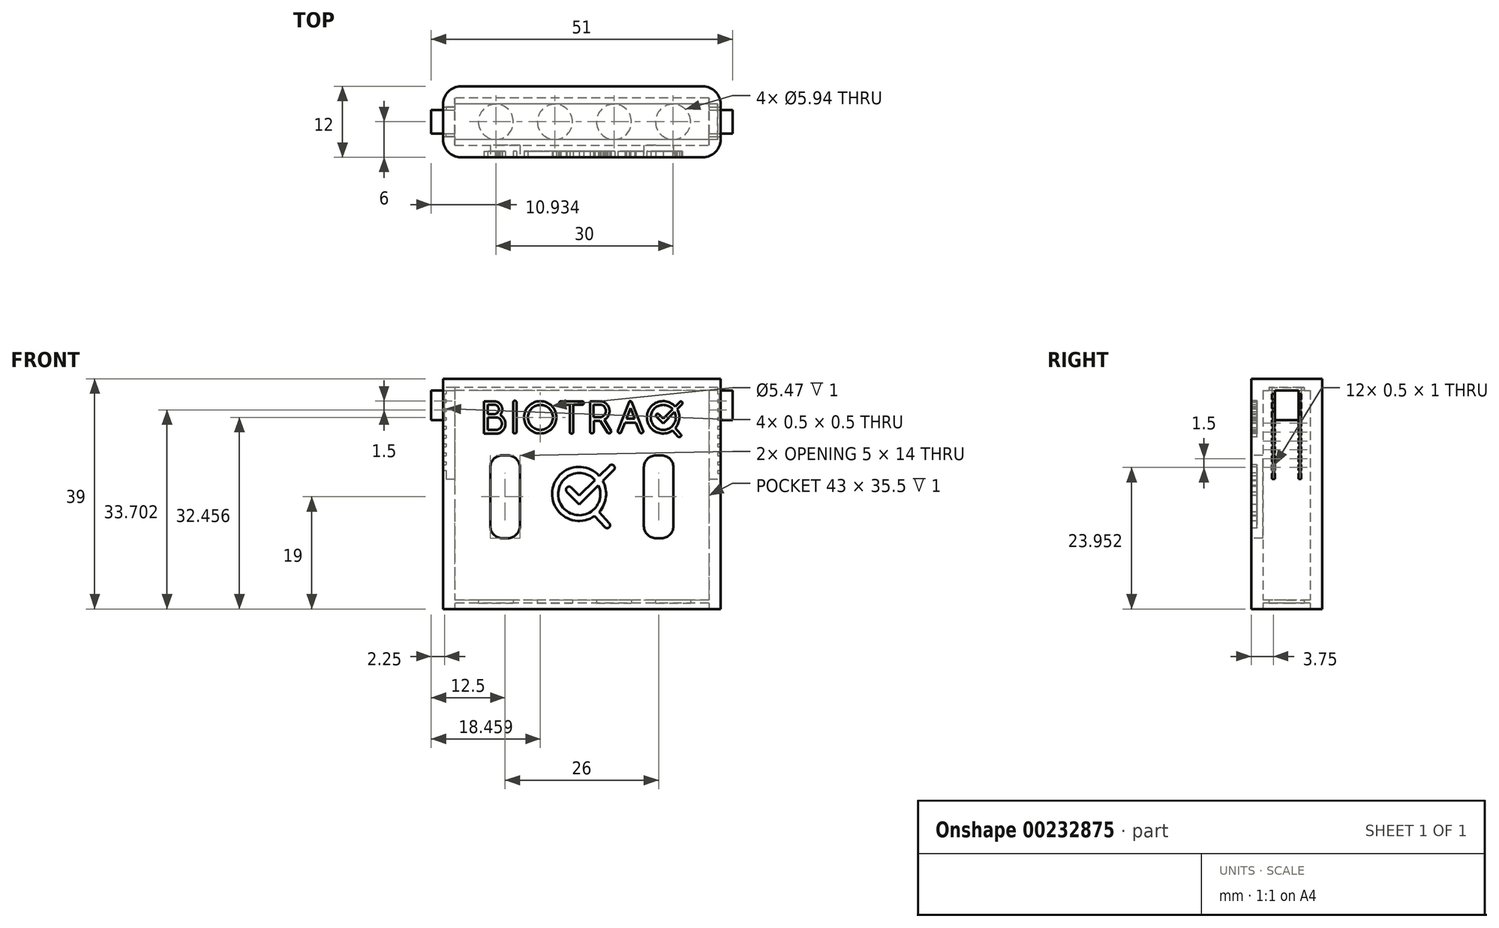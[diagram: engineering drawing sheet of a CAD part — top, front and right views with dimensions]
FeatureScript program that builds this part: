
annotation { "Feature Type Name" : "Feature", "Feature Type Description" : "" }
export const myFeature = defineFeature(function(context is Context, id is Id, definition is map)
    precondition{}
    {
        {
            var Q0;
            Q0=qCreatedBy(makeId("Front.planeOp"),FACE);
            var sketch = newSketch(context, id + "F0", { "sketchPlane" : qUnion([Q0])});
            skLineSegment(sketch, "E0.bottom", {"start": v(-47, 0) * mm, "end": v(0, 0) * mm});
            skLineSegment(sketch, "E0.top", {"start": v(-47, -37) * mm, "end": v(0, -37) * mm});
            skLineSegment(sketch, "E0.left", {"start": v(-47, 0) * mm, "end": v(-47, -37) * mm});
            skLineSegment(sketch, "E0.right", {"start": v(0, 0) * mm, "end": v(0, -37) * mm});
            skSolve(sketch);
        }
        {
            var Q0;
            Q0 = qSketchRegion(id + "F0", true);
            extrude(context, id + "F1", {"entities" : qUnion([Q0]), "depth" : 12 * mm});
        }
        {
            var Q0;
            Q0=makeQuery(id+"F1.opExtrude","SWEPT_FACE",FACE,{"disambiguationData":[OSD([sQuery(id+"F0.wireOp",EDGE,"E0.bottom")])]});
            shell(context, id + "F2", {"entities" : qUnion([Q0]), "thickness" : 2 * mm});
        }
        {
            var Q0;
            Q0=makeQuery(id+"F1.opExtrude","CAP_FACE",FACE,{"disambiguationData":[OSD([sQuery(id+"F0.wireOp",EDGE,"E0.bottom"),sQuery(id+"F0.wireOp",EDGE,"E0.top"),sQuery(id+"F0.wireOp",EDGE,"E0.left"),sQuery(id+"F0.wireOp",EDGE,"E0.right")])],"isStart":false});
            var sketch = newSketch(context, id + "F3", { "sketchPlane" : qUnion([Q0])});
            skLineSegment(sketch, "E1.bottom", {"start": v(-8, -11) * mm, "end": v(-13, -11) * mm});
            skLineSegment(sketch, "E1.top", {"start": v(-8, -25) * mm, "end": v(-13, -25) * mm});
            skLineSegment(sketch, "E1.left", {"start": v(-8, -11) * mm, "end": v(-8, -25) * mm});
            skLineSegment(sketch, "E1.right", {"start": v(-13, -11) * mm, "end": v(-13, -25) * mm});
            skLineSegment(sketch, "E2", {"start": v(-23.5, 0) * mm, "end": v(-23.5, -37) * mm, "construction": true});
            skLineSegment(sketch, "E3.MirrorCS", {"start": v(-39, -11) * mm, "end": v(-34, -11) * mm});
            skLineSegment(sketch, "E4.MirrorCS", {"start": v(-39, -25) * mm, "end": v(-34, -25) * mm});
            skLineSegment(sketch, "E5.MirrorCS", {"start": v(-39, -11) * mm, "end": v(-39, -25) * mm});
            skLineSegment(sketch, "E6.MirrorCS", {"start": v(-34, -11) * mm, "end": v(-34, -25) * mm});
            skSolve(sketch);
        }
        {
            var Q0;
            Q0 = qSketchRegion(id + "F3", true);
            extrude(context, id + "F4", {"entities" : qUnion([Q0]), "operationType" : NewBodyOperationType.REMOVE, "endBound" : BoundingType.UP_TO_NEXT, "oppositeDirection" : true, "depth" : 25 * mm});
        }
        {
            var Q0;
            Q0=makeQuery(id+"F4.boolean.opBoolean","COPY",EDGE,{"derivedFrom":makeQuery(id+"F4.opExtrude","SWEPT_EDGE",EDGE,{"disambiguationData":[OSD([sQuery(id+"F3.wireOp",EDGE,"E1.bottom"),sQuery(id+"F3.wireOp",EDGE,"E1.left")])]})});
            var Q1;
            Q1=makeQuery(id+"F4.boolean.opBoolean","COPY",EDGE,{"derivedFrom":makeQuery(id+"F4.opExtrude","SWEPT_EDGE",EDGE,{"disambiguationData":[OSD([sQuery(id+"F3.wireOp",EDGE,"E1.bottom"),sQuery(id+"F3.wireOp",EDGE,"E1.right")])]})});
            var Q2;
            Q2=makeQuery(id+"F4.boolean.opBoolean","COPY",EDGE,{"derivedFrom":makeQuery(id+"F4.opExtrude","SWEPT_EDGE",EDGE,{"disambiguationData":[OSD([sQuery(id+"F3.wireOp",EDGE,"E1.top"),sQuery(id+"F3.wireOp",EDGE,"E1.left")])]})});
            var Q3;
            Q3=makeQuery(id+"F4.boolean.opBoolean","COPY",EDGE,{"derivedFrom":makeQuery(id+"F4.opExtrude","SWEPT_EDGE",EDGE,{"disambiguationData":[OSD([sQuery(id+"F3.wireOp",EDGE,"E1.top"),sQuery(id+"F3.wireOp",EDGE,"E1.right")])]})});
            var Q4;
            Q4=makeQuery(id+"F4.boolean.opBoolean","COPY",EDGE,{"derivedFrom":makeQuery(id+"F4.opExtrude","SWEPT_EDGE",EDGE,{"disambiguationData":[OSD([sQuery(id+"F3.wireOp",EDGE,"E4.MirrorCS"),sQuery(id+"F3.wireOp",EDGE,"E5.MirrorCS")])]})});
            var Q5;
            Q5=makeQuery(id+"F4.boolean.opBoolean","COPY",EDGE,{"derivedFrom":makeQuery(id+"F4.opExtrude","SWEPT_EDGE",EDGE,{"disambiguationData":[OSD([sQuery(id+"F3.wireOp",EDGE,"E4.MirrorCS"),sQuery(id+"F3.wireOp",EDGE,"E6.MirrorCS")])]})});
            var Q6;
            Q6=makeQuery(id+"F4.boolean.opBoolean","COPY",EDGE,{"derivedFrom":makeQuery(id+"F4.opExtrude","SWEPT_EDGE",EDGE,{"disambiguationData":[OSD([sQuery(id+"F3.wireOp",EDGE,"E3.MirrorCS"),sQuery(id+"F3.wireOp",EDGE,"E6.MirrorCS")])]})});
            var Q7;
            Q7=makeQuery(id+"F4.boolean.opBoolean","COPY",EDGE,{"derivedFrom":makeQuery(id+"F4.opExtrude","SWEPT_EDGE",EDGE,{"disambiguationData":[OSD([sQuery(id+"F3.wireOp",EDGE,"E3.MirrorCS"),sQuery(id+"F3.wireOp",EDGE,"E5.MirrorCS")])]})});
            fillet(context, id + "F5", {"entities" : qUnion([Q0, Q1, Q2, Q3, Q4, Q5, Q6, Q7]), "radius" : 2 * mm, "tangentPropagation" : true, "allowEdgeOverflow" : false});
        }
        {
            var Q0;
            Q0=makeQuery(id+"F2.opShell","OFFSET_FACE",FACE,{"disambiguationData":[OSD([sQuery(id+"F0.wireOp",EDGE,"E0.left")])]});
            var sketch = newSketch(context, id + "F6", { "sketchPlane" : qUnion([Q0])});
            skLineSegment(sketch, "E7.bottom", {"start": v(-8.5, 0) * mm, "end": v(-8, 0) * mm});
            skLineSegment(sketch, "E7.top", {"start": v(-8.5, -15) * mm, "end": v(-8, -15) * mm});
            skLineSegment(sketch, "E7.left", {"start": v(-8.5, 0) * mm, "end": v(-8.5, -15) * mm});
            skLineSegment(sketch, "E7.right", {"start": v(-8, 0) * mm, "end": v(-8, -15) * mm});
            skLineSegment(sketch, "E8", {"start": v(-6, 0) * mm, "end": v(-6, -17.86) * mm, "construction": true});
            skPoint(sketch, "E8.endSnap0", {"position": v(-6, 0) * mm});
            skLineSegment(sketch, "E9.MirrorCS", {"start": v(-3.5, -15) * mm, "end": v(-4, -15) * mm});
            skLineSegment(sketch, "E10.MirrorCS", {"start": v(-3.5, 0) * mm, "end": v(-3.5, -15) * mm});
            skLineSegment(sketch, "E11.MirrorCS", {"start": v(-3.5, 0) * mm, "end": v(-4, 0) * mm});
            skLineSegment(sketch, "E12.MirrorCS", {"start": v(-4, 0) * mm, "end": v(-4, -15) * mm});
            skSolve(sketch);
        }
        {
            var Q0;
            Q0=makeQuery(id+"F6.imprint","IMPRINT",FACE,{"disambiguationData":[TD([[makeQuery(id+"F6.imprint","IMPRINT",EDGE,{"derivedFrom":sQuery(id+"F6.wireOp",EDGE,"E7.bottom")}),-1.0]])]});
            var Q1;
            Q1=makeQuery(id+"F6.imprint","IMPRINT",FACE,{"disambiguationData":[TD([[makeQuery(id+"F6.imprint","IMPRINT",EDGE,{"derivedFrom":sQuery(id+"F6.wireOp",EDGE,"E9.MirrorCS")}),-1.0]])]});
            extrude(context, id + "F7", {"entities" : qUnion([Q0, Q1]), "operationType" : NewBodyOperationType.REMOVE, "endBound" : BoundingType.THROUGH_ALL, "oppositeDirection" : true, "depth" : 25 * mm, "hasSecondDirection" : true, "secondDirectionOppositeDirection" : false, "secondDirectionDepth" : 63.9 * mm});
        }
        {
            var Q0;
            Q0=makeQuery(id+"F1.opExtrude","SWEPT_FACE",FACE,{"disambiguationData":[OSD([sQuery(id+"F0.wireOp",EDGE,"E0.left")])]});
            var sketch = newSketch(context, id + "F8", { "sketchPlane" : qUnion([Q0])});
            skLineSegment(sketch, "E13.bottom", {"start": v(4, 0) * mm, "end": v(8, 0) * mm});
            skLineSegment(sketch, "E13.top", {"start": v(4, -5) * mm, "end": v(8, -5) * mm});
            skLineSegment(sketch, "E13.left", {"start": v(4, 0) * mm, "end": v(4, -5) * mm});
            skLineSegment(sketch, "E13.right", {"start": v(8, 0) * mm, "end": v(8, -5) * mm});
            skSolve(sketch);
        }
        {
            var Q0;
            Q0=makeQuery(id+"F8.imprint","IMPRINT",FACE,{"disambiguationData":[TD([[makeQuery(id+"F8.imprint","IMPRINT",EDGE,{"derivedFrom":sQuery(id+"F8.wireOp",EDGE,"E13.bottom")}),1.0]])]});
            extrude(context, id + "F9", {"entities" : qUnion([Q0]), "operationType" : NewBodyOperationType.ADD, "depth" : 2 * mm});
        }
        {
            var Q0;
            Q0=makeQuery(id+"F1.opExtrude","SWEPT_FACE",FACE,{"disambiguationData":[OSD([sQuery(id+"F0.wireOp",EDGE,"E0.right")])]});
            var sketch = newSketch(context, id + "F10", { "sketchPlane" : qUnion([Q0])});
            skLineSegment(sketch, "E14.bottom", {"start": v(-8, 0) * mm, "end": v(-4, 0) * mm});
            skLineSegment(sketch, "E14.top", {"start": v(-8, -5) * mm, "end": v(-4, -5) * mm});
            skLineSegment(sketch, "E14.left", {"start": v(-8, 0) * mm, "end": v(-8, -5) * mm});
            skLineSegment(sketch, "E14.right", {"start": v(-4, 0) * mm, "end": v(-4, -5) * mm});
            skSolve(sketch);
        }
        {
            var Q0;
            Q0 = qSketchRegion(id + "F10", true);
            extrude(context, id + "F11", {"entities" : qUnion([Q0]), "operationType" : NewBodyOperationType.ADD, "depth" : 2 * mm});
        }
        {
            var Q0;
            {var subQ0=sQuery(id+"F0.wireOp",EDGE,"E0.right");Q0=makeQuery(id+"F7.boolean.opBoolean","COPY",FACE,{"disambiguationData":[TD([makeQuery(id+"F1.opExtrude","SWEPT_FACE",FACE,{"disambiguationData":[OSD([subQ0])]})])],"derivedFrom":makeQuery(id+"F7.opExtrude","SWEPT_FACE",FACE,{"disambiguationData":[OSD([sQuery(id+"F6.wireOp",EDGE,"E7.left")])]})});}
            var sketch = newSketch(context, id + "F12", { "sketchPlane" : qUnion([Q0])});
            skLineSegment(sketch, "E15.bottom", {"start": v(0.5, 0) * mm, "end": v(0, 0) * mm});
            skLineSegment(sketch, "E15.top", {"start": v(0.5, -14.05) * mm, "end": v(0, -14.05) * mm});
            skLineSegment(sketch, "E15.left", {"start": v(0.5, 0) * mm, "end": v(0.5, -14.05) * mm});
            skLineSegment(sketch, "E15.right", {"start": v(0, 0) * mm, "end": v(0, -14.05) * mm});
            skSolve(sketch);
        }
        {
            var Q0;
            Q0=makeQuery(id+"F12.imprint","IMPRINT",FACE,{"disambiguationData":[TD([[makeQuery(id+"F12.imprint","IMPRINT",EDGE,{"derivedFrom":sQuery(id+"F12.wireOp",EDGE,"E15.bottom")}),1.0]])]});
            extrude(context, id + "F13", {"entities" : qUnion([Q0]), "operationType" : NewBodyOperationType.ADD, "depth" : 6.03 * mm});
        }
        {
            var Q0;
            {var subQ0=sQuery(id+"F0.wireOp",EDGE,"E0.left");Q0=makeQuery(id+"F7.boolean.opBoolean","COPY",FACE,{"disambiguationData":[TD([makeQuery(id+"F1.opExtrude","SWEPT_FACE",FACE,{"disambiguationData":[OSD([subQ0])]})])],"derivedFrom":makeQuery(id+"F7.opExtrude","SWEPT_FACE",FACE,{"disambiguationData":[OSD([sQuery(id+"F6.wireOp",EDGE,"E7.left")])]})});}
            var sketch = newSketch(context, id + "F14", { "sketchPlane" : qUnion([Q0])});
            skLineSegment(sketch, "E16.bottom", {"start": v(46.5, 0) * mm, "end": v(47, 0) * mm});
            skLineSegment(sketch, "E16.top", {"start": v(46.5, -34.82) * mm, "end": v(47, -34.82) * mm});
            skLineSegment(sketch, "E16.left", {"start": v(46.5, 0) * mm, "end": v(46.5, -34.82) * mm});
            skLineSegment(sketch, "E16.right", {"start": v(47, 0) * mm, "end": v(47, -34.82) * mm});
            skSolve(sketch);
        }
        {
            var Q0;
            {var subQ0=sQuery(id+"F14.wireOp",EDGE,"E16.bottom");Q0=makeQuery(id+"F14.imprint","IMPRINT",FACE,{"disambiguationData":[TD([[makeQuery(id+"F14.imprint","IMPRINT",EDGE,{"derivedFrom":subQ0}),1.0]])]});}
            extrude(context, id + "F15", {"entities" : qUnion([Q0]), "operationType" : NewBodyOperationType.ADD, "depth" : 7 * mm});
        }
        {
            var Q0;
            {var subQ0=sQuery(id+"F0.wireOp",EDGE,"E0.right");var subQ1=makeQuery(id+"F1.opExtrude","SWEPT_FACE",FACE,{"disambiguationData":[OSD([subQ0])]});var subQ2=makeQuery(id+"F2.opShell","OFFSET_FACE",FACE,{"disambiguationData":[OSD([subQ0])]});var subQ3=makeQuery(id+"F7.opExtrude","SWEPT_FACE",FACE,{"disambiguationData":[OSD([sQuery(id+"F6.wireOp",EDGE,"E7.right")])]});var subQ4=makeQuery(id+"F7.opExtrude","SWEPT_FACE",FACE,{"disambiguationData":[OSD([sQuery(id+"F6.wireOp",EDGE,"E12.MirrorCS")])]});var subQ5=sQuery(id+"F0.wireOp",EDGE,"E0.bottom");var subQ6=makeQuery(id+"F1.opExtrude","SWEPT_FACE",FACE,{"disambiguationData":[OSD([subQ5])]});var subQ7=sQuery(id+"F0.wireOp",EDGE,"E0.left");var subQ8=sQuery(id+"F0.wireOp",EDGE,"E0.top");var subQ9=makeQuery(id+"F1.opExtrude","CAP_FACE",FACE,{"disambiguationData":[OSD([subQ5,subQ8,subQ7,subQ0])],"isStart":false});var subQ10=makeQuery(id+"F1.opExtrude","SWEPT_FACE",FACE,{"disambiguationData":[OSD([subQ7])]});var subQ11=makeQuery(id+"F2.opShell","OFFSET_FACE",FACE,{"disambiguationData":[OSD([subQ7])]});var subQ12=makeQuery(id+"F1.opExtrude","CAP_FACE",FACE,{"disambiguationData":[OSD([subQ5,subQ8,subQ7,subQ0])],"isStart":true});Q0=makeQuery(id+"F15.boolean.opBoolean","MERGE",FACE,{"derivedFrom":[makeQuery(id+"F9.boolean.opBoolean","MERGE",FACE,{"derivedFrom":[makeQuery(id+"F7.boolean.opBoolean","SPLIT",FACE,{"disambiguationData":[TD([subQ10,subQ11,subQ3,subQ4])],"derivedFrom":subQ6}),makeQuery(id+"F9.opExtrude","SWEPT_FACE",FACE,{"disambiguationData":[OSD([sQuery(id+"F8.wireOp",EDGE,"E13.bottom")])]})]}),makeQuery(id+"F13.boolean.opBoolean","MERGE",FACE,{"derivedFrom":[makeQuery(id+"F7.boolean.opBoolean","SPLIT",FACE,{"disambiguationData":[TD([subQ12,subQ10,subQ1,makeQuery(id+"F2.opShell","OFFSET_FACE",FACE,{"disambiguationData":[OSD([subQ5,subQ8,subQ7,subQ0]),TDD([subQ12])]}),subQ11,subQ2,makeQuery(id+"F7.opExtrude","SWEPT_FACE",FACE,{"disambiguationData":[OSD([sQuery(id+"F6.wireOp",EDGE,"E10.MirrorCS")])]})])],"derivedFrom":subQ6}),makeQuery(id+"F7.boolean.opBoolean","SPLIT",FACE,{"disambiguationData":[TD([subQ9,subQ10,subQ1,makeQuery(id+"F2.opShell","OFFSET_FACE",FACE,{"disambiguationData":[OSD([subQ5,subQ8,subQ7,subQ0]),TDD([subQ9])]}),subQ11,subQ2,makeQuery(id+"F7.opExtrude","SWEPT_FACE",FACE,{"disambiguationData":[OSD([sQuery(id+"F6.wireOp",EDGE,"E7.left")])]})])],"derivedFrom":subQ6}),makeQuery(id+"F11.boolean.opBoolean","MERGE",FACE,{"derivedFrom":[makeQuery(id+"F7.boolean.opBoolean","SPLIT",FACE,{"disambiguationData":[TD([subQ1,subQ2,subQ3,subQ4])],"derivedFrom":subQ6}),makeQuery(id+"F11.opExtrude","SWEPT_FACE",FACE,{"disambiguationData":[OSD([sQuery(id+"F10.wireOp",EDGE,"E14.bottom")])]})]}),makeQuery(id+"F13.opExtrude","SWEPT_FACE",FACE,{"disambiguationData":[OSD([sQuery(id+"F12.wireOp",EDGE,"E15.bottom")])]})]}),makeQuery(id+"F15.opExtrude","SWEPT_FACE",FACE,{"disambiguationData":[OSD([sQuery(id+"F14.wireOp",EDGE,"E16.bottom")])]})]});}
            var sketch = newSketch(context, id + "F16", { "sketchPlane" : qUnion([Q0])});
            skLineSegment(sketch, "E17.bottom", {"start": v(-47, 0) * mm, "end": v(0, 0) * mm});
            skLineSegment(sketch, "E17.top", {"start": v(-47, -12) * mm, "end": v(0, -12) * mm});
            skLineSegment(sketch, "E17.left", {"start": v(-47, 0) * mm, "end": v(-47, -12) * mm});
            skLineSegment(sketch, "E17.right", {"start": v(0, 0) * mm, "end": v(0, -12) * mm});
            skSolve(sketch);
        }
        {
            var Q0;
            Q0 = qSketchRegion(id + "F16", true);
            extrude(context, id + "F17", {"entities" : qUnion([Q0]), "operationType" : NewBodyOperationType.ADD, "depth" : 2 * mm});
        }
        {
            var Q0;
            Q0=makeQuery(id+"F2.opShell","OFFSET_FACE",FACE,{"disambiguationData":[OSD([sQuery(id+"F0.wireOp",EDGE,"E0.top")])]});
            var sketch = newSketch(context, id + "F18", { "sketchPlane" : qUnion([Q0])});
            skLineSegment(sketch, "E18.bottom", {"start": v(-45, -2) * mm, "end": v(-2, -2) * mm});
            skLineSegment(sketch, "E18.top", {"start": v(-45, -10) * mm, "end": v(-2, -10) * mm});
            skLineSegment(sketch, "E18.left", {"start": v(-45, -2) * mm, "end": v(-45, -10) * mm});
            skLineSegment(sketch, "E18.right", {"start": v(-2, -2) * mm, "end": v(-2, -10) * mm});
            skSolve(sketch);
        }
        {
            var Q0;
            Q0 = qSketchRegion(id + "F18", true);
            extrude(context, id + "F19", {"entities" : qUnion([Q0]), "operationType" : NewBodyOperationType.REMOVE, "oppositeDirection" : true, "depth" : 25 * mm});
        }
        {
            var Q0;
            {var subQ0=sQuery(id+"F0.wireOp",EDGE,"E0.right");var subQ1=sQuery(id+"F0.wireOp",EDGE,"E0.left");var subQ2=sQuery(id+"F0.wireOp",EDGE,"E0.top");var subQ3=sQuery(id+"F0.wireOp",EDGE,"E0.bottom");Q0=makeQuery(id+"F19.boolean.opBoolean","MERGE",FACE,{"derivedFrom":[makeQuery(id+"F2.opShell","OFFSET_FACE",FACE,{"disambiguationData":[OSD([subQ3,subQ2,subQ1,subQ0]),TDD([makeQuery(id+"F1.opExtrude","CAP_FACE",FACE,{"disambiguationData":[OSD([subQ3,subQ2,subQ1,subQ0])],"isStart":false})])]}),makeQuery(id+"F19.opExtrude","SWEPT_FACE",FACE,{"disambiguationData":[OSD([sQuery(id+"F18.wireOp",EDGE,"E18.top")])]})]});}
            var sketch = newSketch(context, id + "F20", { "sketchPlane" : qUnion([Q0])});
            skLineSegment(sketch, "E19.bottom", {"start": v(2, -35.5) * mm, "end": v(45, -35.5) * mm});
            skLineSegment(sketch, "E19.top", {"start": v(2, -36) * mm, "end": v(45, -36) * mm});
            skLineSegment(sketch, "E19.left", {"start": v(2, -35.5) * mm, "end": v(2, -36) * mm});
            skLineSegment(sketch, "E19.right", {"start": v(45, -35.5) * mm, "end": v(45, -36) * mm});
            skLineSegment(sketch, "E20.1.0.0", {"start": v(2, -34) * mm, "end": v(45, -34) * mm});
            skLineSegment(sketch, "E20.1.0.1", {"start": v(2, -33.5) * mm, "end": v(45, -33.5) * mm});
            skLineSegment(sketch, "E20.1.0.2", {"start": v(45, -33.5) * mm, "end": v(45, -34) * mm});
            skLineSegment(sketch, "E20.1.0.3", {"start": v(2, -33.5) * mm, "end": v(2, -34) * mm});
            skLineSegment(sketch, "E20.2.0.0", {"start": v(2.02, -32) * mm, "end": v(45.02, -32) * mm});
            skLineSegment(sketch, "E20.2.0.1", {"start": v(2.02, -31.5) * mm, "end": v(45.02, -31.5) * mm});
            skLineSegment(sketch, "E20.2.0.2", {"start": v(45.02, -31.5) * mm, "end": v(45.02, -32) * mm});
            skLineSegment(sketch, "E20.2.0.3", {"start": v(2.02, -31.5) * mm, "end": v(2.02, -32) * mm});
            skLineSegment(sketch, "E20.direction1", {"start": v(2, -36) * mm, "end": v(2, -34) * mm, "construction": true});
            skSolve(sketch);
        }
        {
            var Q0;
            Q0=makeQuery(id+"F20.imprint","IMPRINT",FACE,{"disambiguationData":[TD([[makeQuery(id+"F20.imprint","IMPRINT",EDGE,{"derivedFrom":sQuery(id+"F20.wireOp",EDGE,"E19.bottom")}),-1.0]])]});
            extrude(context, id + "F21", {"entities" : qUnion([Q0]), "operationType" : NewBodyOperationType.ADD, "depth" : 8.2 * mm});
        }
        {
            var Q0;
            {var subQ0=sQuery(id+"F8.wireOp",EDGE,"E13.right");var subQ4=sQuery(id+"F0.wireOp",EDGE,"E0.left");var subQ5=makeQuery(id+"F1.opExtrude","SWEPT_FACE",FACE,{"disambiguationData":[OSD([subQ4])]});Q0=makeQuery(id+"F15.boolean.opBoolean","SPLIT",FACE,{"disambiguationData":[TD([subQ5])],"derivedFrom":makeQuery(id+"F9.boolean.opBoolean","MERGE",FACE,{"derivedFrom":[makeQuery(id+"F7.boolean.opBoolean","COPY",FACE,{"disambiguationData":[TD([subQ5])],"derivedFrom":makeQuery(id+"F7.opExtrude","SWEPT_FACE",FACE,{"disambiguationData":[OSD([sQuery(id+"F6.wireOp",EDGE,"E7.right")])]})}),makeQuery(id+"F9.opExtrude","SWEPT_FACE",FACE,{"disambiguationData":[OSD([subQ0])]})]})});}
            var sketch = newSketch(context, id + "F22", { "sketchPlane" : qUnion([Q0])});
            skLineSegment(sketch, "E21", {"start": v(-49, 0) * mm, "end": v(-49, -5) * mm});
            skLineSegment(sketch, "E22", {"start": v(-49, -5) * mm, "end": v(-48, -5) * mm});
            skLineSegment(sketch, "E23", {"start": v(-48, -5) * mm, "end": v(-48, -4.5) * mm});
            skLineSegment(sketch, "E24", {"start": v(-48, -4.5) * mm, "end": v(-48.5, -4.5) * mm});
            skLineSegment(sketch, "E25", {"start": v(-48.5, -4.5) * mm, "end": v(-48.5, -0.5) * mm});
            skLineSegment(sketch, "E26", {"start": v(-48.5, -0.5) * mm, "end": v(-48, -0.5) * mm});
            skLineSegment(sketch, "E27", {"start": v(-48, -0.5) * mm, "end": v(-48, 0) * mm});
            skLineSegment(sketch, "E28", {"start": v(-48, 0) * mm, "end": v(-49, 0) * mm});
            skLineSegment(sketch, "E29", {"start": v(0, 0) * mm, "end": v(-47, 0) * mm});
            skLineSegment(sketch, "E30", {"start": v(-23.5, 0) * mm, "end": v(-23.5, -24.1) * mm});
            skPoint(sketch, "E30.endSnap0", {"position": v(-23.5, 0) * mm});
            skLineSegment(sketch, "E31.MirrorCS", {"start": v(1, 0) * mm, "end": v(2, 0) * mm});
            skLineSegment(sketch, "E32.MirrorCS", {"start": v(1, -0.5) * mm, "end": v(1, 0) * mm});
            skLineSegment(sketch, "E33.MirrorCS", {"start": v(1.5, -0.5) * mm, "end": v(1, -0.5) * mm});
            skLineSegment(sketch, "E34.MirrorCS", {"start": v(2, -5) * mm, "end": v(1, -5) * mm});
            skLineSegment(sketch, "E35.MirrorCS", {"start": v(1, -5) * mm, "end": v(1, -4.5) * mm});
            skLineSegment(sketch, "E36.MirrorCS", {"start": v(1, -4.5) * mm, "end": v(1.5, -4.5) * mm});
            skLineSegment(sketch, "E37.MirrorCS", {"start": v(1.5, -4.5) * mm, "end": v(1.5, -0.5) * mm});
            skLineSegment(sketch, "E38.MirrorCS", {"start": v(2, 0) * mm, "end": v(2, -5) * mm});
            skSolve(sketch);
        }
        {
            var Q0;
            Q0=makeQuery(id+"F17.boolean.opBoolean","MERGE",EDGE,{"derivedFrom":[makeQuery(id+"F1.opExtrude","CAP_EDGE",EDGE,{"disambiguationData":[OSD([sQuery(id+"F0.wireOp",EDGE,"E0.left")])],"isStart":true}),makeQuery(id+"F17.opExtrude","SWEPT_EDGE",EDGE,{"disambiguationData":[OSD([sQuery(id+"F16.wireOp",EDGE,"E17.bottom"),sQuery(id+"F16.wireOp",EDGE,"E17.left")])]})]});
            var Q1;
            Q1=makeQuery(id+"F17.boolean.opBoolean","MERGE",EDGE,{"derivedFrom":[makeQuery(id+"F1.opExtrude","CAP_EDGE",EDGE,{"disambiguationData":[OSD([sQuery(id+"F0.wireOp",EDGE,"E0.left")])],"isStart":false}),makeQuery(id+"F17.opExtrude","SWEPT_EDGE",EDGE,{"disambiguationData":[OSD([sQuery(id+"F16.wireOp",EDGE,"E17.top"),sQuery(id+"F16.wireOp",EDGE,"E17.left")])]})]});
            var Q2;
            Q2=makeQuery(id+"F17.boolean.opBoolean","MERGE",EDGE,{"derivedFrom":[makeQuery(id+"F1.opExtrude","CAP_EDGE",EDGE,{"disambiguationData":[OSD([sQuery(id+"F0.wireOp",EDGE,"E0.right")])],"isStart":false}),makeQuery(id+"F17.opExtrude","SWEPT_EDGE",EDGE,{"disambiguationData":[OSD([sQuery(id+"F16.wireOp",EDGE,"E17.top"),sQuery(id+"F16.wireOp",EDGE,"E17.right")])]})]});
            var Q3;
            Q3=makeQuery(id+"F17.boolean.opBoolean","MERGE",EDGE,{"derivedFrom":[makeQuery(id+"F1.opExtrude","CAP_EDGE",EDGE,{"disambiguationData":[OSD([sQuery(id+"F0.wireOp",EDGE,"E0.right")])],"isStart":true}),makeQuery(id+"F17.opExtrude","SWEPT_EDGE",EDGE,{"disambiguationData":[OSD([sQuery(id+"F16.wireOp",EDGE,"E17.bottom"),sQuery(id+"F16.wireOp",EDGE,"E17.right")])]})]});
            fillet(context, id + "F23", {"entities" : qUnion([Q0, Q1, Q2, Q3]), "radius" : 3 * mm, "tangentPropagation" : true, "allowEdgeOverflow" : false});
        }
        {
            var Q0;
            Q0=makeQuery(id+"F17.boolean.opBoolean","MERGE",FACE,{"derivedFrom":[makeQuery(id+"F1.opExtrude","CAP_FACE",FACE,{"disambiguationData":[OSD([sQuery(id+"F0.wireOp",EDGE,"E0.bottom"),sQuery(id+"F0.wireOp",EDGE,"E0.top"),sQuery(id+"F0.wireOp",EDGE,"E0.left"),sQuery(id+"F0.wireOp",EDGE,"E0.right")])],"isStart":false}),makeQuery(id+"F17.opExtrude","SWEPT_FACE",FACE,{"disambiguationData":[OSD([sQuery(id+"F16.wireOp",EDGE,"E17.top")])]})]});
            var sketch = newSketch(context, id + "F24", { "sketchPlane" : qUnion([Q0])});
            skCircle(sketch, "E39", {"center": v(-23.97, -17.51) * mm, "radius": 4.57 * mm});
            skPoint(sketch, "E39.first.point", {"position": v(-25.64, -13.26) * mm});
            skPoint(sketch, "E39.second.point", {"position": v(-24.6, -22.04) * mm});
            skPoint(sketch, "E39.third.point", {"position": v(-19.4, -17.78) * mm});
            skCircle(sketch, "E40", {"center": v(-23.94, -17.54) * mm, "radius": 3.58 * mm});
            skPoint(sketch, "E40.first.point", {"position": v(-25.17, -14.18) * mm});
            skPoint(sketch, "E40.second.point", {"position": v(-20.6, -18.81) * mm});
            skPoint(sketch, "E40.third.point", {"position": v(-25.44, -20.8) * mm});
            skLineSegment(sketch, "E41", {"start": v(-23.97, -17.8) * mm, "end": v(-18.83, -12.73) * mm});
            skLineSegment(sketch, "E42", {"start": v(-23.97, -17.8) * mm, "end": v(-25.3, -16.44) * mm});
            skLineSegment(sketch, "E43", {"start": v(-26.02, -17.19) * mm, "end": v(-23.97, -19.28) * mm});
            skLineSegment(sketch, "E44", {"start": v(-23.97, -19.28) * mm, "end": v(-18.1, -13.48) * mm});
            skArc(sketch, "E45", {"start": v(-18.1, -13.48) * mm, "mid": v(-18.09, -12.74) * mm, "end": v(-18.83, -12.73) * mm});
            skLineSegment(sketch, "E46", {"start": v(-21.02, -14.02) * mm, "end": v(-21.73, -14.73) * mm});
            skLineSegment(sketch, "E47", {"start": v(-19.7, -15.86) * mm, "end": v(-20.48, -16.63) * mm});
            skLineSegment(sketch, "E48", {"start": v(-40.07, -1.87) * mm, "end": v(-40.07, -7.3) * mm});
            skLineSegment(sketch, "E49", {"start": v(-40.07, -7.3) * mm, "end": v(-37.72, -7.3) * mm});
            skLineSegment(sketch, "E50", {"start": v(-40.07, -1.87) * mm, "end": v(-38.04, -1.87) * mm});
            skLineSegment(sketch, "E51", {"start": v(-39.47, -2.43) * mm, "end": v(-39.47, -3.98) * mm});
            skLineSegment(sketch, "E52", {"start": v(-39.47, -3.98) * mm, "end": v(-38.14, -3.98) * mm});
            skLineSegment(sketch, "E53", {"start": v(-39.47, -2.43) * mm, "end": v(-38.13, -2.43) * mm});
            skLineSegment(sketch, "E54", {"start": v(-37.82, -4.57) * mm, "end": v(-39.47, -4.57) * mm});
            skLineSegment(sketch, "E55", {"start": v(-39.47, -4.57) * mm, "end": v(-39.47, -6.66) * mm});
            skArc(sketch, "E56", {"start": v(-37.33, -4.15) * mm, "mid": v(-37.03, -2.8) * mm, "end": v(-38.04, -1.87) * mm});
            skArc(sketch, "E57", {"start": v(-38.14, -3.98) * mm, "mid": v(-37.56, -3.21) * mm, "end": v(-38.13, -2.43) * mm});
            skArc(sketch, "E58", {"start": v(-37.72, -7.3) * mm, "mid": v(-36.46, -5.85) * mm, "end": v(-37.33, -4.15) * mm});
            skArc(sketch, "E59", {"start": v(-37.82, -6.65) * mm, "mid": v(-37.04, -5.61) * mm, "end": v(-37.82, -4.57) * mm});
            skLineSegment(sketch, "E60", {"start": v(-39.47, -6.66) * mm, "end": v(-37.82, -6.65) * mm});
            skLineSegment(sketch, "E61", {"start": v(-35.15, -2.02) * mm, "end": v(-35.15, -7.1) * mm});
            skLineSegment(sketch, "E62", {"start": v(-34.55, -2.03) * mm, "end": v(-34.55, -7.1) * mm});
            skArc(sketch, "E63", {"start": v(-34.55, -2.03) * mm, "mid": v(-34.84, -1.74) * mm, "end": v(-35.15, -2.02) * mm});
            skArc(sketch, "E64", {"start": v(-35.15, -7.1) * mm, "mid": v(-34.85, -7.26) * mm, "end": v(-34.55, -7.1) * mm});
            skCircle(sketch, "E65", {"center": v(-30.54, -4.54) * mm, "radius": 2.74 * mm});
            skPoint(sketch, "E65.first.point", {"position": v(-31.6, -2.02) * mm});
            skPoint(sketch, "E65.second.point", {"position": v(-27.96, -5.44) * mm});
            skPoint(sketch, "E65.third.point", {"position": v(-31.76, -7) * mm});
            skCircle(sketch, "E66", {"center": v(-30.52, -4.56) * mm, "radius": 2.12 * mm});
            skPoint(sketch, "E66.first.point", {"position": v(-31, -2.5) * mm});
            skPoint(sketch, "E66.second.point", {"position": v(-28.64, -5.53) * mm});
            skPoint(sketch, "E66.third.point", {"position": v(-31.07, -6.6) * mm});
            skLineSegment(sketch, "E67", {"start": v(-27.05, -1.82) * mm, "end": v(-23.45, -1.82) * mm});
            skLineSegment(sketch, "E68", {"start": v(-23.45, -1.82) * mm, "end": v(-23.45, -2.4) * mm});
            skLineSegment(sketch, "E69", {"start": v(-23.45, -2.4) * mm, "end": v(-24.94, -2.4) * mm});
            skLineSegment(sketch, "E70", {"start": v(-24.94, -2.4) * mm, "end": v(-24.94, -7.15) * mm});
            skLineSegment(sketch, "E71", {"start": v(-24.94, -7.15) * mm, "end": v(-25.53, -7.15) * mm});
            skLineSegment(sketch, "E72", {"start": v(-25.53, -7.15) * mm, "end": v(-25.53, -2.4) * mm});
            skLineSegment(sketch, "E73", {"start": v(-25.53, -2.4) * mm, "end": v(-27.05, -2.4) * mm});
            skLineSegment(sketch, "E74", {"start": v(-27.05, -2.4) * mm, "end": v(-27.05, -1.82) * mm});
            skArc(sketch, "E75", {"start": v(-27.05, -1.82) * mm, "mid": v(-27.34, -2.12) * mm, "end": v(-27.05, -2.4) * mm});
            skArc(sketch, "E76", {"start": v(-23.45, -2.4) * mm, "mid": v(-23.16, -2.12) * mm, "end": v(-23.45, -1.82) * mm});
            skArc(sketch, "E77", {"start": v(-25.53, -7.15) * mm, "mid": v(-25.24, -7.3) * mm, "end": v(-24.94, -7.15) * mm});
            skLineSegment(sketch, "E78", {"start": v(-22.12, -1.82) * mm, "end": v(-22.12, -7.08) * mm});
            skLineSegment(sketch, "E79", {"start": v(-21.5, -7.08) * mm, "end": v(-21.5, -5.15) * mm});
            skLineSegment(sketch, "E80", {"start": v(-21.5, -5.15) * mm, "end": v(-20.36, -5.15) * mm});
            skLineSegment(sketch, "E81", {"start": v(-20.36, -5.15) * mm, "end": v(-19.1, -7.2) * mm});
            skLineSegment(sketch, "E82", {"start": v(-18.57, -6.86) * mm, "end": v(-19.73, -4.97) * mm});
            skLineSegment(sketch, "E83", {"start": v(-20.3, -4.52) * mm, "end": v(-21.56, -4.52) * mm});
            skLineSegment(sketch, "E84", {"start": v(-21.56, -4.52) * mm, "end": v(-21.56, -2.4) * mm});
            skLineSegment(sketch, "E85", {"start": v(-21.56, -2.4) * mm, "end": v(-20.24, -2.4) * mm});
            skLineSegment(sketch, "E86", {"start": v(-20.24, -1.82) * mm, "end": v(-22.12, -1.82) * mm});
            skArc(sketch, "E87", {"start": v(-19.73, -4.97) * mm, "mid": v(-18.84, -3.21) * mm, "end": v(-20.24, -1.82) * mm});
            skArc(sketch, "E88", {"start": v(-20.3, -4.52) * mm, "mid": v(-19.44, -3.48) * mm, "end": v(-20.24, -2.4) * mm});
            skArc(sketch, "E89", {"start": v(-19.1, -7.2) * mm, "mid": v(-18.72, -7.22) * mm, "end": v(-18.57, -6.86) * mm});
            skArc(sketch, "E90", {"start": v(-22.12, -7.08) * mm, "mid": v(-21.8, -7.26) * mm, "end": v(-21.5, -7.08) * mm});
            skLineSegment(sketch, "E91", {"start": v(-15.53, -1.97) * mm, "end": v(-17.4, -6.78) * mm});
            skLineSegment(sketch, "E92", {"start": v(-16.8, -7) * mm, "end": v(-16.2, -5.43) * mm});
            skLineSegment(sketch, "E93", {"start": v(-16.2, -5.43) * mm, "end": v(-14.34, -5.43) * mm});
            skLineSegment(sketch, "E94", {"start": v(-14.34, -5.43) * mm, "end": v(-13.7, -7.04) * mm});
            skLineSegment(sketch, "E95", {"start": v(-13.14, -6.81) * mm, "end": v(-15.08, -1.96) * mm});
            skLineSegment(sketch, "E96", {"start": v(-15.25, -2.97) * mm, "end": v(-14.55, -4.78) * mm});
            skLineSegment(sketch, "E97", {"start": v(-14.55, -4.78) * mm, "end": v(-15.98, -4.78) * mm});
            skLineSegment(sketch, "E98", {"start": v(-15.98, -4.78) * mm, "end": v(-15.25, -2.97) * mm});
            skArc(sketch, "E99", {"start": v(-15.08, -1.96) * mm, "mid": v(-15.3, -1.8) * mm, "end": v(-15.53, -1.97) * mm});
            skArc(sketch, "E100", {"start": v(-13.7, -7.04) * mm, "mid": v(-13.3, -7.2) * mm, "end": v(-13.14, -6.81) * mm});
            skArc(sketch, "E101", {"start": v(-17.4, -6.78) * mm, "mid": v(-17.22, -7.2) * mm, "end": v(-16.8, -7) * mm});
            skCircle(sketch, "E102", {"center": v(-9.72, -4.55) * mm, "radius": 2.11 * mm});
            skPoint(sketch, "E102.first.point", {"position": v(-10.41, -2.56) * mm});
            skPoint(sketch, "E102.second.point", {"position": v(-7.61, -4.62) * mm});
            skPoint(sketch, "E102.third.point", {"position": v(-10.66, -6.44) * mm});
            skCircle(sketch, "E103", {"center": v(-9.75, -4.54) * mm, "radius": 2.75 * mm});
            skPoint(sketch, "E103.first.point", {"position": v(-11.18, -2.2) * mm});
            skPoint(sketch, "E103.second.point", {"position": v(-7.1, -5.28) * mm});
            skPoint(sketch, "E103.third.point", {"position": v(-10.66, -7.13) * mm});
            skLineSegment(sketch, "E104", {"start": v(-9.73, -5.57) * mm, "end": v(-6.55, -2.34) * mm});
            skLineSegment(sketch, "E105", {"start": v(-6.94, -1.95) * mm, "end": v(-9.72, -4.76) * mm});
            skLineSegment(sketch, "E106", {"start": v(-9.72, -4.76) * mm, "end": v(-10.47, -4.02) * mm});
            skLineSegment(sketch, "E107", {"start": v(-10.88, -4.43) * mm, "end": v(-9.73, -5.57) * mm});
            skArc(sketch, "E108", {"start": v(-10.47, -4.02) * mm, "mid": v(-10.88, -4.02) * mm, "end": v(-10.88, -4.43) * mm});
            skArc(sketch, "E109", {"start": v(-6.55, -2.34) * mm, "mid": v(-6.55, -1.95) * mm, "end": v(-6.94, -1.95) * mm});
            skLineSegment(sketch, "E110", {"start": v(-8.02, -2.4) * mm, "end": v(-8.44, -2.87) * mm});
            skLineSegment(sketch, "E111", {"start": v(-7.68, -4) * mm, "end": v(-7.2, -3.51) * mm});
            skArc(sketch, "E112", {"start": v(-25.3, -16.44) * mm, "mid": v(-26.05, -16.44) * mm, "end": v(-26.02, -17.19) * mm});
            skLineSegment(sketch, "E113", {"start": v(-21.33, -21.25) * mm, "end": v(-19.6, -23.15) * mm});
            skLineSegment(sketch, "E114", {"start": v(-18.85, -22.47) * mm, "end": v(-20.57, -20.58) * mm});
            skArc(sketch, "E115", {"start": v(-19.6, -23.15) * mm, "mid": v(-18.88, -23.18) * mm, "end": v(-18.85, -22.47) * mm});
            skLineSegment(sketch, "E116", {"start": v(-7.7, -6.37) * mm, "end": v(-6.77, -7.38) * mm});
            skLineSegment(sketch, "E117", {"start": v(-7.24, -7.8) * mm, "end": v(-8.16, -6.79) * mm});
            skArc(sketch, "E118", {"start": v(-7.24, -7.8) * mm, "mid": v(-6.8, -7.82) * mm, "end": v(-6.77, -7.38) * mm});
            skSolve(sketch);
        }
        {
            var Q0;
            Q0 = qSketchRegion(id + "F24", true);
            var Q1;
            {var subQ0=sQuery(id+"F24.wireOp",EDGE,"E42");Q1=makeQuery(id+"F24.imprint","IMPRINT",FACE,{"disambiguationData":[TD([[makeQuery(id+"F24.imprint","IMPRINT",EDGE,{"derivedFrom":subQ0}),1.0]])]});}
            var Q2;
            {var subQ0=sQuery(id+"F24.wireOp",EDGE,"E106");Q2=makeQuery(id+"F24.imprint","IMPRINT",FACE,{"disambiguationData":[TD([[makeQuery(id+"F24.imprint","IMPRINT",EDGE,{"derivedFrom":subQ0}),1.0]])]});}
            extrude(context, id + "F25", {"entities" : qUnion([Q0, Q1, Q2]), "operationType" : NewBodyOperationType.REMOVE, "oppositeDirection" : true, "depth" : 1 * mm});
        }
        {
            var Q0;
            Q0=makeQuery(id+"F17.boolean.opBoolean","MERGE",FACE,{"derivedFrom":[makeQuery(id+"F15.boolean.opBoolean","MERGE",FACE,{"derivedFrom":[makeQuery(id+"F1.opExtrude","SWEPT_FACE",FACE,{"disambiguationData":[OSD([sQuery(id+"F0.wireOp",EDGE,"E0.left")])]}),makeQuery(id+"F15.opExtrude","SWEPT_FACE",FACE,{"disambiguationData":[OSD([sQuery(id+"F14.wireOp",EDGE,"E16.right")])]})]}),makeQuery(id+"F17.opExtrude","SWEPT_FACE",FACE,{"disambiguationData":[OSD([sQuery(id+"F16.wireOp",EDGE,"E17.left")])]})]});
            var sketch = newSketch(context, id + "F26", { "sketchPlane" : qUnion([Q0])});
            skLineSegment(sketch, "E119.bottom", {"start": v(3, 0) * mm, "end": v(9, 0) * mm});
            skLineSegment(sketch, "E119.top", {"start": v(3, 0.5) * mm, "end": v(9, 0.5) * mm});
            skLineSegment(sketch, "E119.left", {"start": v(3, 0) * mm, "end": v(3, 0.5) * mm});
            skLineSegment(sketch, "E119.right", {"start": v(9, 0) * mm, "end": v(9, 0.5) * mm});
            skSolve(sketch);
        }
        {
            var Q0;
            Q0 = qSketchRegion(id + "F26", true);
            extrude(context, id + "F27", {"entities" : qUnion([Q0]), "operationType" : NewBodyOperationType.REMOVE, "endBound" : BoundingType.UP_TO_NEXT, "oppositeDirection" : true, "depth" : 25 * mm});
        }
        {
            var Q0;
            {var subQ2=sQuery(id+"F10.wireOp",EDGE,"E14.bottom");var subQ3=sQuery(id+"F0.wireOp",EDGE,"E0.bottom");var subQ4=makeQuery(id+"F1.opExtrude","SWEPT_FACE",FACE,{"disambiguationData":[OSD([subQ3])]});var subQ5=sQuery(id+"F0.wireOp",EDGE,"E0.right");var subQ6=makeQuery(id+"F2.opShell","OFFSET_FACE",FACE,{"disambiguationData":[OSD([subQ5])]});var subQ7=makeQuery(id+"F1.opExtrude","SWEPT_FACE",FACE,{"disambiguationData":[OSD([subQ5])]});var subQ8=makeQuery(id+"F7.opExtrude","SWEPT_FACE",FACE,{"disambiguationData":[OSD([sQuery(id+"F6.wireOp",EDGE,"E12.MirrorCS")])]});var subQ9=makeQuery(id+"F7.opExtrude","SWEPT_FACE",FACE,{"disambiguationData":[OSD([sQuery(id+"F6.wireOp",EDGE,"E7.right")])]});var subQ10=subQ4;var subQ11=sQuery(id+"F0.wireOp",EDGE,"E0.left");var subQ12=sQuery(id+"F0.wireOp",EDGE,"E0.top");var subQ13=makeQuery(id+"F1.opExtrude","CAP_FACE",FACE,{"disambiguationData":[OSD([subQ3,subQ12,subQ11,subQ5])],"isStart":false});var subQ14=makeQuery(id+"F1.opExtrude","SWEPT_FACE",FACE,{"disambiguationData":[OSD([subQ11])]});var subQ15=makeQuery(id+"F2.opShell","OFFSET_FACE",FACE,{"disambiguationData":[OSD([subQ11])]});var subQ16=makeQuery(id+"F1.opExtrude","CAP_FACE",FACE,{"disambiguationData":[OSD([subQ3,subQ12,subQ11,subQ5])],"isStart":true});Q0=makeQuery(id+"F27.boolean.opBoolean","MERGE",FACE,{"derivedFrom":[makeQuery(id+"FunIcHRDmyxUIi6_1.boolean.opBoolean","MERGE",FACE,{"derivedFrom":[makeQuery(id+"F17.boolean.opBoolean","SPLIT",FACE,{"disambiguationData":[TD([subQ7])],"derivedFrom":makeQuery(id+"F15.boolean.opBoolean","MERGE",FACE,{"derivedFrom":[makeQuery(id+"F9.boolean.opBoolean","MERGE",FACE,{"derivedFrom":[makeQuery(id+"F7.boolean.opBoolean","SPLIT",FACE,{"disambiguationData":[TD([subQ14,subQ15,subQ9,subQ8])],"derivedFrom":subQ10}),makeQuery(id+"F9.opExtrude","SWEPT_FACE",FACE,{"disambiguationData":[OSD([sQuery(id+"F8.wireOp",EDGE,"E13.bottom")])]})]}),makeQuery(id+"F13.boolean.opBoolean","MERGE",FACE,{"derivedFrom":[makeQuery(id+"F7.boolean.opBoolean","SPLIT",FACE,{"disambiguationData":[TD([subQ16,subQ14,subQ7,makeQuery(id+"F2.opShell","OFFSET_FACE",FACE,{"disambiguationData":[OSD([subQ3,subQ12,subQ11,subQ5]),TDD([subQ16])]}),subQ15,subQ6,makeQuery(id+"F7.opExtrude","SWEPT_FACE",FACE,{"disambiguationData":[OSD([sQuery(id+"F6.wireOp",EDGE,"E10.MirrorCS")])]})])],"derivedFrom":subQ10}),makeQuery(id+"F7.boolean.opBoolean","SPLIT",FACE,{"disambiguationData":[TD([subQ13,subQ14,subQ7,makeQuery(id+"F2.opShell","OFFSET_FACE",FACE,{"disambiguationData":[OSD([subQ3,subQ12,subQ11,subQ5]),TDD([subQ13])]}),subQ15,subQ6,makeQuery(id+"F7.opExtrude","SWEPT_FACE",FACE,{"disambiguationData":[OSD([sQuery(id+"F6.wireOp",EDGE,"E7.left")])]})])],"derivedFrom":subQ10}),makeQuery(id+"F11.boolean.opBoolean","MERGE",FACE,{"derivedFrom":[makeQuery(id+"F7.boolean.opBoolean","SPLIT",FACE,{"disambiguationData":[TD([subQ7,subQ6,subQ9,subQ8])],"derivedFrom":subQ10}),makeQuery(id+"F11.opExtrude","SWEPT_FACE",FACE,{"disambiguationData":[OSD([subQ2])]})]}),makeQuery(id+"F13.opExtrude","SWEPT_FACE",FACE,{"disambiguationData":[OSD([sQuery(id+"F12.wireOp",EDGE,"E15.bottom")])]})]}),makeQuery(id+"F15.opExtrude","SWEPT_FACE",FACE,{"disambiguationData":[OSD([sQuery(id+"F14.wireOp",EDGE,"E16.bottom")])]})]})}),makeQuery(id+"FunIcHRDmyxUIi6_1.opExtrude","SWEPT_FACE",FACE,{"disambiguationData":[OSD([sQuery(id+"F22.wireOp",EDGE,"E31.MirrorCS")])]})]}),makeQuery(id+"F27.opExtrude","SWEPT_FACE",FACE,{"disambiguationData":[OSD([sQuery(id+"F26.wireOp",EDGE,"E119.bottom")])]})]});}
            var sketch = newSketch(context, id + "F28", { "sketchPlane" : qUnion([Q0])});
            skLineSegment(sketch, "E120.bottom", {"start": v(0, -3) * mm, "end": v(-0.5, -3) * mm});
            skLineSegment(sketch, "E120.top", {"start": v(0, -9) * mm, "end": v(-0.5, -9) * mm});
            skLineSegment(sketch, "E120.left", {"start": v(0, -3) * mm, "end": v(0, -9) * mm});
            skLineSegment(sketch, "E120.right", {"start": v(-0.5, -3) * mm, "end": v(-0.5, -9) * mm});
            skSolve(sketch);
        }
        {
            var Q0;
            Q0 = qSketchRegion(id + "F28", true);
            extrude(context, id + "F29", {"entities" : qUnion([Q0]), "operationType" : NewBodyOperationType.ADD, "endBound" : BoundingType.UP_TO_NEXT, "depth" : 25 * mm});
        }
        {
            var Q0;
            Q0=makeQuery(id+"F21.opExtrude","SWEPT_FACE",FACE,{"disambiguationData":[OSD([sQuery(id+"F20.wireOp",EDGE,"E19.top")])]});
            var sketch = newSketch(context, id + "F30", { "sketchPlane" : qUnion([Q0])});
            skCircle(sketch, "E121", {"center": v(-38.07, 6) * mm, "radius": 2.97 * mm});
            skPoint(sketch, "E121.centerSnap0", {"position": v(-45, 6) * mm});
            skLineSegment(sketch, "E122", {"start": v(-45, 6) * mm, "end": v(-26.83, 6) * mm});
            skCircle(sketch, "E123.1.0.0", {"center": v(-28.07, 6) * mm, "radius": 2.97 * mm});
            skCircle(sketch, "E123.2.0.0", {"center": v(-18.07, 6) * mm, "radius": 2.97 * mm});
            skCircle(sketch, "E123.3.0.0", {"center": v(-8.07, 6) * mm, "radius": 2.97 * mm});
            skLineSegment(sketch, "E123.direction1", {"start": v(-38.07, 6) * mm, "end": v(-28.07, 6) * mm, "construction": true});
            skSolve(sketch);
        }
        {
            var Q0;
            {var subQ0=sQuery(id+"F30.wireOp",EDGE,"E122");var subQ1=sQuery(id+"F30.wireOp",EDGE,"E121");var subQ2=makeQuery(id+"F30.imprint","INTERSECT",VERTEX,{"disambiguationData":[OD(0.0)],"derivedFrom":[subQ1,subQ0]});Q0=makeQuery(id+"F30.imprint","IMPRINT",FACE,{"disambiguationData":[TD([[makeQuery(id+"F30.imprint","IMPRINT",EDGE,{"disambiguationData":[TD([[subQ2,1.0]])],"derivedFrom":subQ1}),1.0]])]});}
            var Q1;
            {var subQ0=sQuery(id+"F30.wireOp",EDGE,"E122");var subQ1=sQuery(id+"F30.wireOp",EDGE,"E121");var subQ2=makeQuery(id+"F30.imprint","INTERSECT",VERTEX,{"disambiguationData":[OD(0.0)],"derivedFrom":[subQ1,subQ0]});Q1=makeQuery(id+"F30.imprint","IMPRINT",FACE,{"disambiguationData":[TD([[makeQuery(id+"F30.imprint","IMPRINT",EDGE,{"disambiguationData":[TD([[subQ2,-1.0]])],"derivedFrom":subQ1}),1.0]])]});}
            var Q2;
            Q2=makeQuery(id+"F30.imprint","IMPRINT",FACE,{"disambiguationData":[TD([[makeQuery(id+"F30.imprint","IMPRINT",EDGE,{"derivedFrom":sQuery(id+"F30.wireOp",EDGE,"E123.1.0.0")}),1.0]])]});
            var Q3;
            Q3=makeQuery(id+"F30.imprint","IMPRINT",FACE,{"disambiguationData":[TD([[makeQuery(id+"F30.imprint","IMPRINT",EDGE,{"derivedFrom":sQuery(id+"F30.wireOp",EDGE,"E123.2.0.0")}),1.0]])]});
            var Q4;
            Q4=makeQuery(id+"F30.imprint","IMPRINT",FACE,{"disambiguationData":[TD([[makeQuery(id+"F30.imprint","IMPRINT",EDGE,{"derivedFrom":sQuery(id+"F30.wireOp",EDGE,"E123.3.0.0")}),1.0]])]});
            extrude(context, id + "F31", {"entities" : qUnion([Q0, Q1, Q2, Q3, Q4]), "operationType" : NewBodyOperationType.REMOVE, "endBound" : BoundingType.UP_TO_NEXT, "oppositeDirection" : true, "depth" : 25 * mm});
        }
        {
            var Q0;
            {var subQ2=sQuery(id+"F8.wireOp",EDGE,"E13.bottom");var subQ3=sQuery(id+"F0.wireOp",EDGE,"E0.bottom");var subQ4=makeQuery(id+"F1.opExtrude","SWEPT_FACE",FACE,{"disambiguationData":[OSD([subQ3])]});var subQ5=sQuery(id+"F0.wireOp",EDGE,"E0.left");var subQ6=makeQuery(id+"F1.opExtrude","SWEPT_FACE",FACE,{"disambiguationData":[OSD([subQ5])]});var subQ7=makeQuery(id+"F2.opShell","OFFSET_FACE",FACE,{"disambiguationData":[OSD([subQ5])]});var subQ8=makeQuery(id+"F7.opExtrude","SWEPT_FACE",FACE,{"disambiguationData":[OSD([sQuery(id+"F6.wireOp",EDGE,"E12.MirrorCS")])]});var subQ9=makeQuery(id+"F7.opExtrude","SWEPT_FACE",FACE,{"disambiguationData":[OSD([sQuery(id+"F6.wireOp",EDGE,"E7.right")])]});var subQ10=sQuery(id+"F0.wireOp",EDGE,"E0.right");var subQ11=makeQuery(id+"F1.opExtrude","SWEPT_FACE",FACE,{"disambiguationData":[OSD([subQ10])]});var subQ12=makeQuery(id+"F2.opShell","OFFSET_FACE",FACE,{"disambiguationData":[OSD([subQ10])]});var subQ13=subQ4;var subQ14=sQuery(id+"F0.wireOp",EDGE,"E0.top");var subQ15=makeQuery(id+"F1.opExtrude","CAP_FACE",FACE,{"disambiguationData":[OSD([subQ3,subQ14,subQ5,subQ10])],"isStart":false});var subQ16=makeQuery(id+"F1.opExtrude","CAP_FACE",FACE,{"disambiguationData":[OSD([subQ3,subQ14,subQ5,subQ10])],"isStart":true});Q0=makeQuery(id+"F27.boolean.opBoolean","MERGE",FACE,{"derivedFrom":[makeQuery(id+"FunIcHRDmyxUIi6_1.boolean.opBoolean","MERGE",FACE,{"derivedFrom":[makeQuery(id+"F17.boolean.opBoolean","SPLIT",FACE,{"disambiguationData":[TD([subQ6])],"derivedFrom":makeQuery(id+"F15.boolean.opBoolean","MERGE",FACE,{"derivedFrom":[makeQuery(id+"F9.boolean.opBoolean","MERGE",FACE,{"derivedFrom":[makeQuery(id+"F7.boolean.opBoolean","SPLIT",FACE,{"disambiguationData":[TD([subQ6,subQ7,subQ9,subQ8])],"derivedFrom":subQ13}),makeQuery(id+"F9.opExtrude","SWEPT_FACE",FACE,{"disambiguationData":[OSD([subQ2])]})]}),makeQuery(id+"F13.boolean.opBoolean","MERGE",FACE,{"derivedFrom":[makeQuery(id+"F7.boolean.opBoolean","SPLIT",FACE,{"disambiguationData":[TD([subQ16,subQ6,subQ11,makeQuery(id+"F2.opShell","OFFSET_FACE",FACE,{"disambiguationData":[OSD([subQ3,subQ14,subQ5,subQ10]),TDD([subQ16])]}),subQ7,subQ12,makeQuery(id+"F7.opExtrude","SWEPT_FACE",FACE,{"disambiguationData":[OSD([sQuery(id+"F6.wireOp",EDGE,"E10.MirrorCS")])]})])],"derivedFrom":subQ13}),makeQuery(id+"F7.boolean.opBoolean","SPLIT",FACE,{"disambiguationData":[TD([subQ15,subQ6,subQ11,makeQuery(id+"F2.opShell","OFFSET_FACE",FACE,{"disambiguationData":[OSD([subQ3,subQ14,subQ5,subQ10]),TDD([subQ15])]}),subQ7,subQ12,makeQuery(id+"F7.opExtrude","SWEPT_FACE",FACE,{"disambiguationData":[OSD([sQuery(id+"F6.wireOp",EDGE,"E7.left")])]})])],"derivedFrom":subQ13}),makeQuery(id+"F11.boolean.opBoolean","MERGE",FACE,{"derivedFrom":[makeQuery(id+"F7.boolean.opBoolean","SPLIT",FACE,{"disambiguationData":[TD([subQ11,subQ12,subQ9,subQ8])],"derivedFrom":subQ13}),makeQuery(id+"F11.opExtrude","SWEPT_FACE",FACE,{"disambiguationData":[OSD([sQuery(id+"F10.wireOp",EDGE,"E14.bottom")])]})]}),makeQuery(id+"F13.opExtrude","SWEPT_FACE",FACE,{"disambiguationData":[OSD([sQuery(id+"F12.wireOp",EDGE,"E15.bottom")])]})]}),makeQuery(id+"F15.opExtrude","SWEPT_FACE",FACE,{"disambiguationData":[OSD([sQuery(id+"F14.wireOp",EDGE,"E16.bottom")])]})]})}),makeQuery(id+"FunIcHRDmyxUIi6_1.opExtrude","SWEPT_FACE",FACE,{"disambiguationData":[OSD([sQuery(id+"F22.wireOp",EDGE,"E28")])]})]}),makeQuery(id+"F27.opExtrude","SWEPT_FACE",FACE,{"disambiguationData":[OSD([sQuery(id+"F26.wireOp",EDGE,"E119.bottom")])]})]});}
            var sketch = newSketch(context, id + "F32", { "sketchPlane" : qUnion([Q0])});
            skLineSegment(sketch, "E124.bottom", {"start": v(-47, -3) * mm, "end": v(-45, -3) * mm});
            skLineSegment(sketch, "E124.top", {"start": v(-47, -3.5) * mm, "end": v(-45, -3.5) * mm});
            skLineSegment(sketch, "E124.left", {"start": v(-47, -3) * mm, "end": v(-47, -3.5) * mm});
            skLineSegment(sketch, "E124.right", {"start": v(-45, -3) * mm, "end": v(-45, -3.5) * mm});
            skLineSegment(sketch, "E125.bottom", {"start": v(-47, -9) * mm, "end": v(-45, -9) * mm});
            skLineSegment(sketch, "E125.top", {"start": v(-47, -8.5) * mm, "end": v(-45, -8.5) * mm});
            skLineSegment(sketch, "E125.left", {"start": v(-47, -9) * mm, "end": v(-47, -8.5) * mm});
            skLineSegment(sketch, "E125.right", {"start": v(-45, -9) * mm, "end": v(-45, -8.5) * mm});
            skSolve(sketch);
        }
        {
            var Q0;
            Q0 = qSketchRegion(id + "F32", true);
            extrude(context, id + "F33", {"entities" : qUnion([Q0]), "operationType" : NewBodyOperationType.ADD, "endBound" : BoundingType.UP_TO_NEXT, "depth" : 1 * mm});
        }
        {
            var Q0;
            {var subQ0=sQuery(id+"F16.wireOp",EDGE,"E17.right");var subQ2=sQuery(id+"F0.wireOp",EDGE,"E0.right");var subQ7=makeQuery(id+"F1.opExtrude","SWEPT_FACE",FACE,{"disambiguationData":[OSD([subQ2])]});var subQ12=makeQuery(id+"F1.opExtrude","SWEPT_FACE",FACE,{"disambiguationData":[OSD([sQuery(id+"F0.wireOp",EDGE,"E0.bottom")])]});var subQ17=makeQuery(id+"F17.boolean.opBoolean","MERGE",FACE,{"derivedFrom":[makeQuery(id+"F13.boolean.opBoolean","MERGE",FACE,{"derivedFrom":[subQ7,makeQuery(id+"F13.opExtrude","SWEPT_FACE",FACE,{"disambiguationData":[OSD([sQuery(id+"F12.wireOp",EDGE,"E15.right")])]})]}),makeQuery(id+"F17.opExtrude","SWEPT_FACE",FACE,{"disambiguationData":[OSD([subQ0])]})]});Q0=makeQuery(id+"F29.boolean.opBoolean","MERGE",FACE,{"derivedFrom":[makeQuery(id+"F27.boolean.opBoolean","SPLIT",FACE,{"disambiguationData":[TD([makeQuery(id+"F27.opExtrude","SWEPT_FACE",FACE,{"disambiguationData":[OSD([sQuery(id+"F26.wireOp",EDGE,"E119.top")])]})])],"derivedFrom":subQ17}),makeQuery(id+"F27.boolean.opBoolean","SPLIT",FACE,{"disambiguationData":[TD([subQ12])],"derivedFrom":subQ17}),makeQuery(id+"F29.opExtrude","SWEPT_FACE",FACE,{"disambiguationData":[OSD([sQuery(id+"F28.wireOp",EDGE,"E120.left")])]})]});}
            var sketch = newSketch(context, id + "F34", { "sketchPlane" : qUnion([Q0])});
            skLineSegment(sketch, "E126.bottom", {"start": v(-4, -13.55) * mm, "end": v(-3.5, -13.55) * mm});
            skLineSegment(sketch, "E126.top", {"start": v(-4, -12.55) * mm, "end": v(-3.5, -12.55) * mm});
            skLineSegment(sketch, "E126.left", {"start": v(-4, -13.55) * mm, "end": v(-4, -12.55) * mm});
            skLineSegment(sketch, "E126.right", {"start": v(-3.5, -13.55) * mm, "end": v(-3.5, -12.55) * mm});
            skLineSegment(sketch, "E127.1.0.0", {"start": v(-4, -11.05) * mm, "end": v(-3.5, -11.05) * mm});
            skLineSegment(sketch, "E127.1.0.1", {"start": v(-4, -12.05) * mm, "end": v(-4, -11.05) * mm});
            skLineSegment(sketch, "E127.1.0.2", {"start": v(-4, -12.05) * mm, "end": v(-3.5, -12.05) * mm});
            skLineSegment(sketch, "E127.1.0.3", {"start": v(-3.5, -12.05) * mm, "end": v(-3.5, -11.05) * mm});
            skLineSegment(sketch, "E127.2.0.0", {"start": v(-4, -9.55) * mm, "end": v(-3.5, -9.55) * mm});
            skLineSegment(sketch, "E127.2.0.1", {"start": v(-4, -10.55) * mm, "end": v(-4, -9.55) * mm});
            skLineSegment(sketch, "E127.2.0.2", {"start": v(-4, -10.55) * mm, "end": v(-3.5, -10.55) * mm});
            skLineSegment(sketch, "E127.2.0.3", {"start": v(-3.5, -10.55) * mm, "end": v(-3.5, -9.55) * mm});
            skLineSegment(sketch, "E127.3.0.0", {"start": v(-4, -8.05) * mm, "end": v(-3.5, -8.05) * mm});
            skLineSegment(sketch, "E127.3.0.1", {"start": v(-4, -9.05) * mm, "end": v(-4, -8.05) * mm});
            skLineSegment(sketch, "E127.3.0.2", {"start": v(-4, -9.05) * mm, "end": v(-3.5, -9.05) * mm});
            skLineSegment(sketch, "E127.3.0.3", {"start": v(-3.5, -9.05) * mm, "end": v(-3.5, -8.05) * mm});
            skLineSegment(sketch, "E127.4.0.0", {"start": v(-4, -6.55) * mm, "end": v(-3.5, -6.55) * mm});
            skLineSegment(sketch, "E127.4.0.1", {"start": v(-4, -7.55) * mm, "end": v(-4, -6.55) * mm});
            skLineSegment(sketch, "E127.4.0.2", {"start": v(-4, -7.55) * mm, "end": v(-3.5, -7.55) * mm});
            skLineSegment(sketch, "E127.4.0.3", {"start": v(-3.5, -7.55) * mm, "end": v(-3.5, -6.55) * mm});
            skLineSegment(sketch, "E127.5.0.0", {"start": v(-4, -5.05) * mm, "end": v(-3.5, -5.05) * mm});
            skLineSegment(sketch, "E127.5.0.1", {"start": v(-4, -6.05) * mm, "end": v(-4, -5.05) * mm});
            skLineSegment(sketch, "E127.5.0.2", {"start": v(-4, -6.05) * mm, "end": v(-3.5, -6.05) * mm});
            skLineSegment(sketch, "E127.5.0.3", {"start": v(-3.5, -6.05) * mm, "end": v(-3.5, -5.05) * mm});
            skLineSegment(sketch, "E127.6.0.0", {"start": v(-4, -3.55) * mm, "end": v(-3.5, -3.55) * mm});
            skLineSegment(sketch, "E127.6.0.1", {"start": v(-4, -4.55) * mm, "end": v(-4, -3.55) * mm});
            skLineSegment(sketch, "E127.6.0.2", {"start": v(-4, -4.55) * mm, "end": v(-3.5, -4.55) * mm});
            skLineSegment(sketch, "E127.6.0.3", {"start": v(-3.5, -4.55) * mm, "end": v(-3.5, -3.55) * mm});
            skLineSegment(sketch, "E127.7.0.0", {"start": v(-4, -2.05) * mm, "end": v(-3.5, -2.05) * mm});
            skLineSegment(sketch, "E127.7.0.1", {"start": v(-4, -3.05) * mm, "end": v(-4, -2.05) * mm});
            skLineSegment(sketch, "E127.7.0.2", {"start": v(-4, -3.05) * mm, "end": v(-3.5, -3.05) * mm});
            skLineSegment(sketch, "E127.7.0.3", {"start": v(-3.5, -3.05) * mm, "end": v(-3.5, -2.05) * mm});
            skLineSegment(sketch, "E127.8.0.0", {"start": v(-4, -0.55) * mm, "end": v(-3.5, -0.55) * mm});
            skLineSegment(sketch, "E127.8.0.1", {"start": v(-4, -1.55) * mm, "end": v(-4, -0.55) * mm});
            skLineSegment(sketch, "E127.8.0.2", {"start": v(-4, -1.55) * mm, "end": v(-3.5, -1.55) * mm});
            skLineSegment(sketch, "E127.8.0.3", {"start": v(-3.5, -1.55) * mm, "end": v(-3.5, -0.55) * mm});
            skLineSegment(sketch, "E127.direction1", {"start": v(-4, -13.55) * mm, "end": v(-4, -12.05) * mm, "construction": true});
            skLineSegment(sketch, "E128", {"start": v(-6, 2) * mm, "end": v(-6, -12.8) * mm, "construction": true});
            skLineSegment(sketch, "E129.MirrorCS", {"start": v(-8, -13.55) * mm, "end": v(-8, -12.55) * mm});
            skLineSegment(sketch, "E130.MirrorCS", {"start": v(-8, -12.55) * mm, "end": v(-8.5, -12.55) * mm});
            skLineSegment(sketch, "E131.MirrorCS", {"start": v(-8, -1.55) * mm, "end": v(-8, -0.55) * mm});
            skLineSegment(sketch, "E132.MirrorCS", {"start": v(-8, -1.55) * mm, "end": v(-8.5, -1.55) * mm});
            skLineSegment(sketch, "E133.MirrorCS", {"start": v(-8, -13.55) * mm, "end": v(-8.5, -13.55) * mm});
            skLineSegment(sketch, "E134.MirrorCS", {"start": v(-8, -4.55) * mm, "end": v(-8.5, -4.55) * mm});
            skLineSegment(sketch, "E135.MirrorCS", {"start": v(-8.5, -1.55) * mm, "end": v(-8.5, -0.55) * mm});
            skLineSegment(sketch, "E136.MirrorCS", {"start": v(-8, -10.55) * mm, "end": v(-8.5, -10.55) * mm});
            skLineSegment(sketch, "E137.MirrorCS", {"start": v(-8, -10.55) * mm, "end": v(-8, -9.55) * mm});
            skLineSegment(sketch, "E138.MirrorCS", {"start": v(-8.5, -9.05) * mm, "end": v(-8.5, -8.05) * mm});
            skLineSegment(sketch, "E139.MirrorCS", {"start": v(-8, -8.05) * mm, "end": v(-8.5, -8.05) * mm});
            skLineSegment(sketch, "E140.MirrorCS", {"start": v(-8.5, -10.55) * mm, "end": v(-8.5, -9.55) * mm});
            skLineSegment(sketch, "E141.MirrorCS", {"start": v(-8, -11.05) * mm, "end": v(-8.5, -11.05) * mm});
            skLineSegment(sketch, "E142.MirrorCS", {"start": v(-8.5, -6.05) * mm, "end": v(-8.5, -5.05) * mm});
            skLineSegment(sketch, "E143.MirrorCS", {"start": v(-8, -6.05) * mm, "end": v(-8, -5.05) * mm});
            skLineSegment(sketch, "E144.MirrorCS", {"start": v(-8.5, -13.55) * mm, "end": v(-8.5, -12.55) * mm});
            skLineSegment(sketch, "E145.MirrorCS", {"start": v(-8, -3.05) * mm, "end": v(-8.5, -3.05) * mm});
            skLineSegment(sketch, "E146.MirrorCS", {"start": v(-8.5, -7.55) * mm, "end": v(-8.5, -6.55) * mm});
            skLineSegment(sketch, "E147.MirrorCS", {"start": v(-8, -7.55) * mm, "end": v(-8.5, -7.55) * mm});
            skLineSegment(sketch, "E148.MirrorCS", {"start": v(-8, -9.55) * mm, "end": v(-8.5, -9.55) * mm});
            skLineSegment(sketch, "E149.MirrorCS", {"start": v(-8, -4.55) * mm, "end": v(-8, -3.55) * mm});
            skLineSegment(sketch, "E150.MirrorCS", {"start": v(-8, -9.05) * mm, "end": v(-8.5, -9.05) * mm});
            skLineSegment(sketch, "E151.MirrorCS", {"start": v(-8, -12.05) * mm, "end": v(-8, -11.05) * mm});
            skLineSegment(sketch, "E152.MirrorCS", {"start": v(-8, -3.05) * mm, "end": v(-8, -2.05) * mm});
            skLineSegment(sketch, "E153.MirrorCS", {"start": v(-8.5, -4.55) * mm, "end": v(-8.5, -3.55) * mm});
            skLineSegment(sketch, "E154.MirrorCS", {"start": v(-8, -5.05) * mm, "end": v(-8.5, -5.05) * mm});
            skLineSegment(sketch, "E155.MirrorCS", {"start": v(-8, -13.55) * mm, "end": v(-8, -12.05) * mm, "construction": true});
            skLineSegment(sketch, "E156.MirrorCS", {"start": v(-8, -9.05) * mm, "end": v(-8, -8.05) * mm});
            skLineSegment(sketch, "E157.MirrorCS", {"start": v(-8, -12.05) * mm, "end": v(-8.5, -12.05) * mm});
            skLineSegment(sketch, "E158.MirrorCS", {"start": v(-8, -0.55) * mm, "end": v(-8.5, -0.55) * mm});
            skLineSegment(sketch, "E159.MirrorCS", {"start": v(-8, -3.55) * mm, "end": v(-8.5, -3.55) * mm});
            skLineSegment(sketch, "E160.MirrorCS", {"start": v(-8, -6.55) * mm, "end": v(-8.5, -6.55) * mm});
            skLineSegment(sketch, "E161.MirrorCS", {"start": v(-8, -7.55) * mm, "end": v(-8, -6.55) * mm});
            skLineSegment(sketch, "E162.MirrorCS", {"start": v(-8, -2.05) * mm, "end": v(-8.5, -2.05) * mm});
            skLineSegment(sketch, "E163.MirrorCS", {"start": v(-8.5, -12.05) * mm, "end": v(-8.5, -11.05) * mm});
            skLineSegment(sketch, "E164.MirrorCS", {"start": v(-8.5, -3.05) * mm, "end": v(-8.5, -2.05) * mm});
            skLineSegment(sketch, "E165.MirrorCS", {"start": v(-8, -6.05) * mm, "end": v(-8.5, -6.05) * mm});
            skSolve(sketch);
        }
        {
            var Q0;
            Q0 = qSketchRegion(id + "F34", true);
            extrude(context, id + "F35", {"entities" : qUnion([Q0]), "operationType" : NewBodyOperationType.REMOVE, "oppositeDirection" : true, "depth" : 47.7 * mm});
        }
    });
